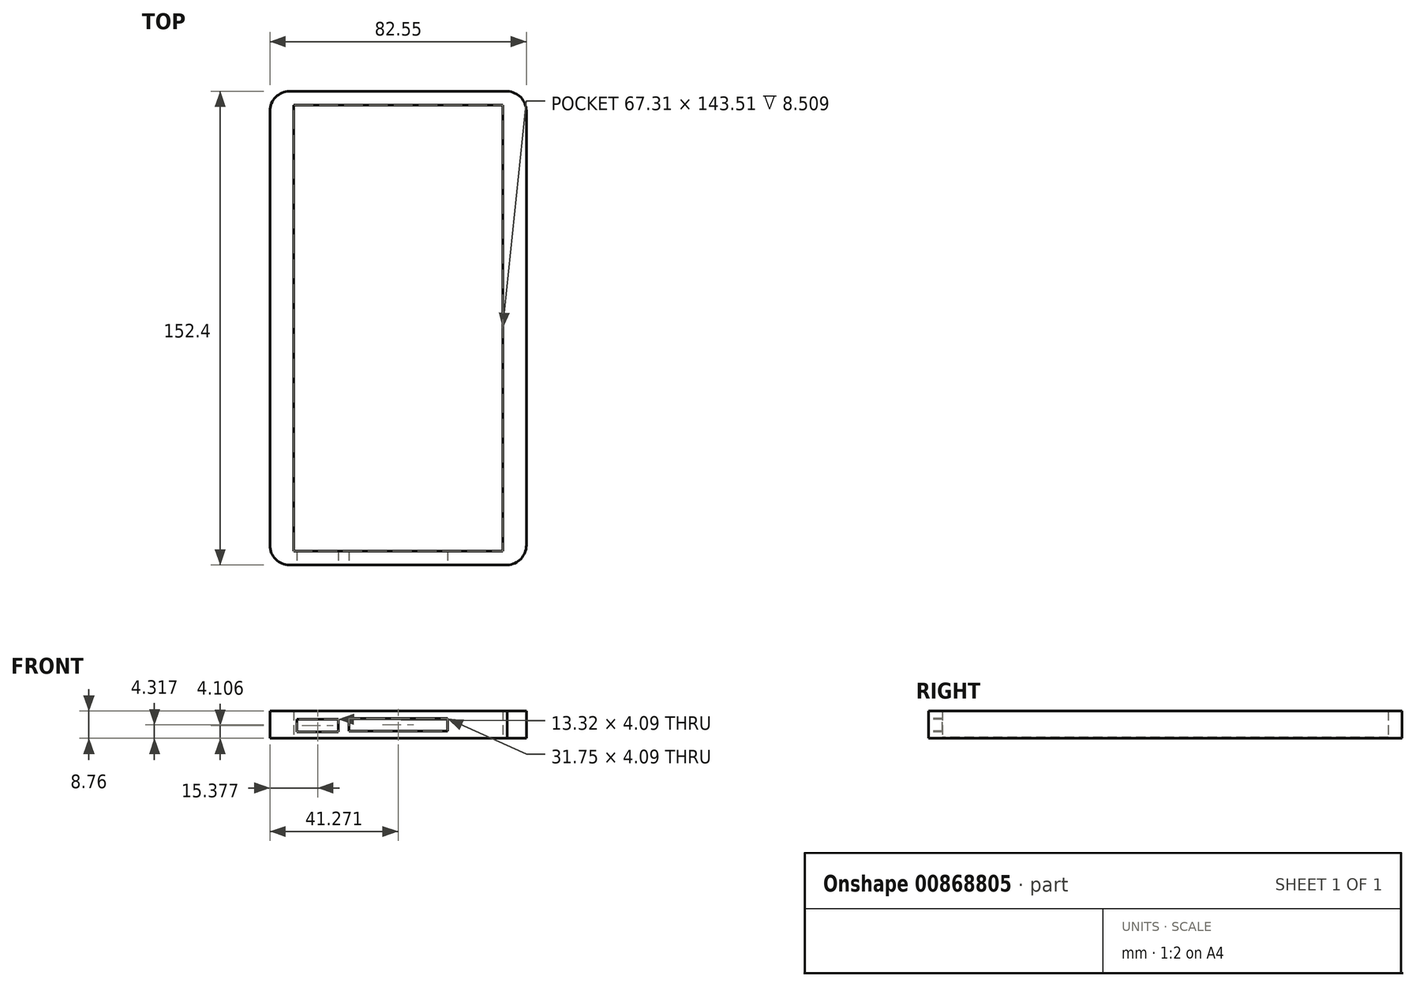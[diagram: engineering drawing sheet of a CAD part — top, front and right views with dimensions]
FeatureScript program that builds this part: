
annotation { "Feature Type Name" : "Feature", "Feature Type Description" : "" }
export const myFeature = defineFeature(function(context is Context, id is Id, definition is map)
    precondition{}
    {
        {
            var Q0;
            Q0=qCreatedBy(makeId("Top.planeOp"),FACE);
            var sketch = newSketch(context, id + "F0", { "sketchPlane" : qUnion([Q0])});
            skLineSegment(sketch, "E0", {"start": v(-46.42, 0) * mm, "end": v(-46.42, 69.85) * mm});
            skLineSegment(sketch, "E1", {"start": v(36.13, 0) * mm, "end": v(36.13, 69.85) * mm});
            skLineSegment(sketch, "E2", {"start": v(30.01, 76.2) * mm, "end": v(-40.07, 76.2) * mm});
            skArc(sketch, "E3", {"start": v(-46.42, 69.85) * mm, "mid": v(-44.56, 74.34) * mm, "end": v(-40.07, 76.2) * mm});
            skArc(sketch, "E4", {"start": v(36.13, 69.85) * mm, "mid": v(34.35, 74.26) * mm, "end": v(30.01, 76.2) * mm});
            skLineSegment(sketch, "E5", {"start": v(-38.8, 71.76) * mm, "end": v(28.5, 71.76) * mm});
            skLineSegment(sketch, "E6", {"start": v(-38.8, 71.76) * mm, "end": v(-38.8, 0) * mm});
            skLineSegment(sketch, "E7", {"start": v(28.5, 71.76) * mm, "end": v(28.5, 0) * mm});
            skLineSegment(sketch, "E8.MirrorCS", {"start": v(-46.42, 0) * mm, "end": v(-46.42, -69.85) * mm});
            skLineSegment(sketch, "E9.MirrorCS", {"start": v(-38.8, -71.76) * mm, "end": v(-38.8, 0) * mm});
            skArc(sketch, "E10.MirrorCS", {"start": v(-46.42, -69.85) * mm, "mid": v(-44.56, -74.34) * mm, "end": v(-40.07, -76.2) * mm});
            skLineSegment(sketch, "E11.MirrorCS", {"start": v(-38.8, -71.76) * mm, "end": v(28.5, -71.76) * mm});
            skLineSegment(sketch, "E12.MirrorCS", {"start": v(30.01, -76.2) * mm, "end": v(-40.07, -76.2) * mm});
            skLineSegment(sketch, "E13.MirrorCS", {"start": v(36.13, 0) * mm, "end": v(36.13, -69.85) * mm});
            skLineSegment(sketch, "E14.MirrorCS", {"start": v(28.5, -71.76) * mm, "end": v(28.5, 0) * mm});
            skArc(sketch, "E15.MirrorCS", {"start": v(36.13, -69.85) * mm, "mid": v(34.35, -74.26) * mm, "end": v(30.01, -76.2) * mm});
            skSolve(sketch);
        }
        {
            var Q0;
            Q0=makeQuery(id+"F0.imprint","IMPRINT",FACE,{"disambiguationData":[TD([[makeQuery(id+"F0.imprint","IMPRINT",EDGE,{"derivedFrom":sQuery(id+"F0.wireOp",EDGE,"E0")}),-1.0]])]});
            var Q1;
            Q1=makeQuery(id+"F0.imprint","IMPRINT",FACE,{"disambiguationData":[TD([[makeQuery(id+"F0.imprint","IMPRINT",EDGE,{"derivedFrom":sQuery(id+"F0.wireOp",EDGE,"E5")}),-1.0]])]});
            extrude(context, id + "F1", {"entities" : qUnion([Q0, Q1]), "oppositeDirection" : true, "depth" : 0.25 * mm, "offsetDistance" : 25.4 * mm});
        }
        {
            var Q0;
            Q0=makeQuery(id+"F0.imprint","IMPRINT",FACE,{"disambiguationData":[TD([[makeQuery(id+"F0.imprint","IMPRINT",EDGE,{"derivedFrom":sQuery(id+"F0.wireOp",EDGE,"E0")}),-1.0]])]});
            extrude(context, id + "F2", {"entities" : qUnion([Q0]), "operationType" : NewBodyOperationType.ADD, "depth" : 8.5 * mm, "offsetDistance" : 25.4 * mm});
        }
        {
            var Q0;
            {var subQ0=sQuery(id+"F0.wireOp",EDGE,"E12.MirrorCS");Q0=makeQuery(id+"F2.boolean.opBoolean","MERGE",FACE,{"derivedFrom":[makeQuery(id+"F1.opExtrude","SWEPT_FACE",FACE,{"disambiguationData":[OSD([subQ0])]}),makeQuery(id+"F2.opExtrude","SWEPT_FACE",FACE,{"disambiguationData":[OSD([subQ0])]})]});}
            var sketch = newSketch(context, id + "F3", { "sketchPlane" : qUnion([Q0])});
            skLineSegment(sketch, "E16.left", {"start": v(-21.02, 6.11) * mm, "end": v(-21.02, 2.02) * mm});
            skLineSegment(sketch, "E17", {"start": v(10.73, 6.11) * mm, "end": v(10.73, 2.02) * mm});
            skLineSegment(sketch, "E18", {"start": v(-21.02, 6.11) * mm, "end": v(10.73, 6.11) * mm});
            skLineSegment(sketch, "E19", {"start": v(-21.02, 2.02) * mm, "end": v(10.73, 2.02) * mm});
            skLineSegment(sketch, "E20.bottom", {"start": v(-37.7, 5.9) * mm, "end": v(-24.38, 5.9) * mm});
            skLineSegment(sketch, "E20.top", {"start": v(-37.7, 1.81) * mm, "end": v(-24.38, 1.81) * mm});
            skLineSegment(sketch, "E20.left", {"start": v(-37.7, 5.9) * mm, "end": v(-37.7, 1.81) * mm});
            skLineSegment(sketch, "E20.right", {"start": v(-24.38, 5.9) * mm, "end": v(-24.38, 1.81) * mm});
            skSolve(sketch);
        }
        {
            var Q0;
            Q0 = qSketchRegion(id + "F3", true);
            extrude(context, id + "F4", {"entities" : qUnion([Q0]), "operationType" : NewBodyOperationType.REMOVE, "oppositeDirection" : true, "depth" : 25.4 * mm, "offsetDistance" : 25.4 * mm});
        }
    });
